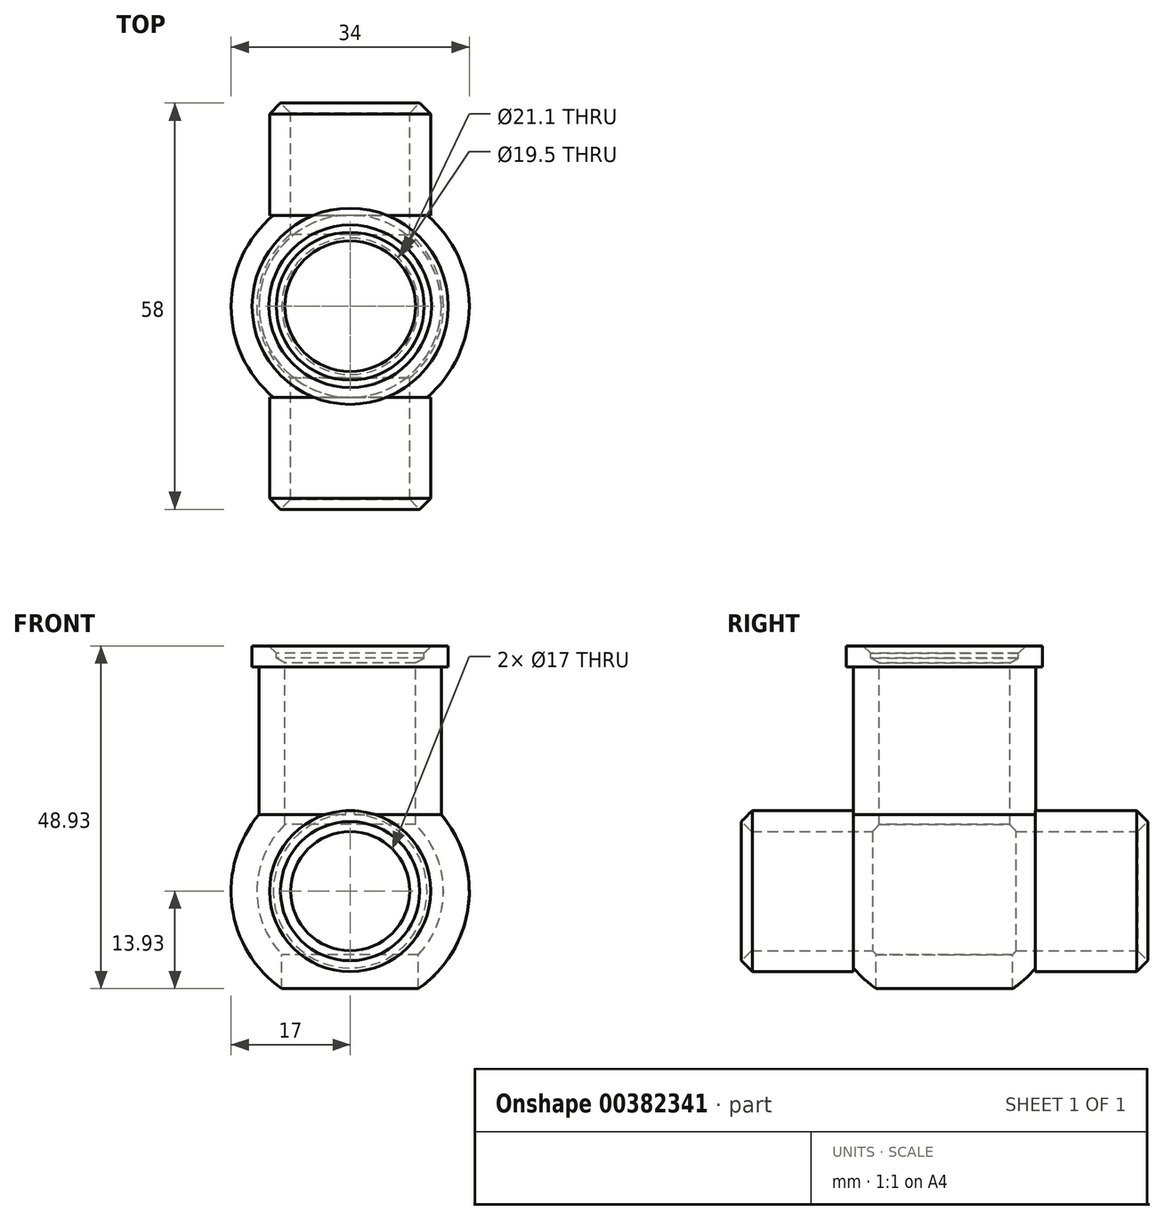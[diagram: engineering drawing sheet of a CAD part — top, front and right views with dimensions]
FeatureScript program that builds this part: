
annotation { "Feature Type Name" : "Feature", "Feature Type Description" : "" }
export const myFeature = defineFeature(function(context is Context, id is Id, definition is map)
    precondition{}
    {
        {
            var Q0;
            Q0=qCreatedBy(makeId("Front.planeOp"),FACE);
            var sketch = newSketch(context, id + "F0", { "sketchPlane" : qUnion([Q0])});
            skArc(sketch, "E0", {"start": v(-9.32, 14.22) * mm, "mid": v(-17, 0.26) * mm, "end": v(-9.75, -13.93) * mm});
            skLineSegment(sketch, "E1", {"start": v(0, 35) * mm, "end": v(0, -13.32) * mm, "construction": true});
            skLineSegment(sketch, "E2", {"start": v(0, 35) * mm, "end": v(-14, 35) * mm});
            skLineSegment(sketch, "E3", {"start": v(-14, 35) * mm, "end": v(-14, 32) * mm});
            skLineSegment(sketch, "E4", {"start": v(-14, 32) * mm, "end": v(-13, 32) * mm});
            skLineSegment(sketch, "E5", {"start": v(-13, 32) * mm, "end": v(-13, 10.95) * mm});
            skLineSegment(sketch, "E6", {"start": v(0, 35) * mm, "end": v(-11.6, 35) * mm});
            skLineSegment(sketch, "E7", {"start": v(-11.6, 35) * mm, "end": v(-10.55, 33.95) * mm});
            skLineSegment(sketch, "E8", {"start": v(-10.55, 33.95) * mm, "end": v(-10.55, 33.25) * mm});
            skLineSegment(sketch, "E9", {"start": v(-10.55, 33.95) * mm, "end": v(0, 33.95) * mm});
            skLineSegment(sketch, "E10", {"start": v(-10.55, 33.25) * mm, "end": v(0, 33.25) * mm});
            skLineSegment(sketch, "E11", {"start": v(0, 32.6) * mm, "end": v(-9.32, 32.6) * mm});
            skLineSegment(sketch, "E12", {"start": v(-10.55, 33.25) * mm, "end": v(-9.32, 32.6) * mm});
            skLineSegment(sketch, "E13", {"start": v(-9.32, 32.6) * mm, "end": v(-9.32, 9.52) * mm});
            skArc(sketch, "E14", {"start": v(-9.32, 9.52) * mm, "mid": v(-13.31, 0.31) * mm, "end": v(-9.75, -9.07) * mm});
            skLineSegment(sketch, "E15", {"start": v(-10.48, 33.21) * mm, "end": v(-10.48, 19.21) * mm});
            skLineSegment(sketch, "E16", {"start": v(-10.48, 19.21) * mm, "end": v(0, 19.21) * mm});
            skLineSegment(sketch, "E17", {"start": v(0, 13.32) * mm, "end": v(0, 17) * mm});
            skLineSegment(sketch, "E18", {"start": v(-9.75, -9.07) * mm, "end": v(-9.75, -13.93) * mm});
            skLineSegment(sketch, "E19.trimOffspring", {"start": v(0, -17) * mm, "end": v(0, -57.86) * mm, "construction": true});
            skSolve(sketch);
        }
        {
            var Q0;
            Q0=qCreatedBy(makeId("Right.planeOp"),FACE);
            var sketch = newSketch(context, id + "F1", { "sketchPlane" : qUnion([Q0])});
            skLineSegment(sketch, "E20", {"start": v(29, 0) * mm, "end": v(-20.36, 0) * mm, "construction": true});
            skLineSegment(sketch, "E21", {"start": v(29, 0) * mm, "end": v(29, 11.5) * mm});
            skLineSegment(sketch, "E22", {"start": v(29, 0) * mm, "end": v(29, -11.5) * mm});
            skLineSegment(sketch, "E23", {"start": v(29, -11.5) * mm, "end": v(0, -11.5) * mm});
            skLineSegment(sketch, "E24", {"start": v(29, 0) * mm, "end": v(29, 8.5) * mm});
            skLineSegment(sketch, "E25", {"start": v(29, 9.93) * mm, "end": v(27.57, 8.5) * mm});
            skLineSegment(sketch, "E26", {"start": v(29, 9.93) * mm, "end": v(27.43, 11.5) * mm});
            skLineSegment(sketch, "E27", {"start": v(27.43, 11.5) * mm, "end": v(0, 11.5) * mm});
            skLineSegment(sketch, "E28", {"start": v(27.57, 8.5) * mm, "end": v(0, 8.5) * mm});
            skLineSegment(sketch, "E29", {"start": v(12.99, 11.5) * mm, "end": v(12.99, 10.97) * mm});
            skArc(sketch, "E30", {"start": v(12.99, 10.97) * mm, "mid": v(13.9, 9.77) * mm, "end": v(14.72, 8.5) * mm});
            skPoint(sketch, "E31", {"position": v(17, 0) * mm});
            skArc(sketch, "E32.MirrorCS", {"start": v(-12.99, 10.97) * mm, "mid": v(-13.9, 9.77) * mm, "end": v(-14.72, 8.5) * mm});
            skLineSegment(sketch, "E33.MirrorCS", {"start": v(-27.43, 11.5) * mm, "end": v(0, 11.5) * mm});
            skLineSegment(sketch, "E34.MirrorCS", {"start": v(-12.99, 11.5) * mm, "end": v(-12.99, 10.97) * mm});
            skLineSegment(sketch, "E35.MirrorCS", {"start": v(-27.57, 8.5) * mm, "end": v(0, 8.5) * mm});
            skLineSegment(sketch, "E36.MirrorCS", {"start": v(-29, 9.93) * mm, "end": v(-27.57, 8.5) * mm});
            skLineSegment(sketch, "E37.MirrorCS", {"start": v(-29, 9.93) * mm, "end": v(-27.43, 11.5) * mm});
            skPoint(sketch, "E38", {"position": v(-20.36, 0) * mm});
            skSolve(sketch);
        }
        {
            var Q0;
            Q0=qSketchRegion(id+"F0",true);
            var Q1;
            Q1=sQuery(id+"F0.wireOp",EDGE,"E1");
            revolve(context, id + "F2", {"entities" : qUnion([Q0]), "axis" : qUnion([Q1]), "revolveType" : RevolveType.FULL});
        }
        {
            var Q0;
            {var subQ1=sQuery(id+"F1.wireOp",EDGE,"E25");Q0=makeQuery(id+"F1.imprint","IMPRINT",FACE,{"disambiguationData":[TD([[makeQuery(id+"F1.imprint","IMPRINT",EDGE,{"derivedFrom":subQ1}),-1.0]])]});}
            var Q1;
            Q1=sQuery(id+"F1.wireOp",EDGE,"E20");
            revolve(context, id + "F3", {"operationType" : NewBodyOperationType.ADD, "entities" : qUnion([Q0]), "axis" : qUnion([Q1]), "revolveType" : RevolveType.FULL});
        }
        {
            var Q0;
            {var subQ1=sQuery(id+"F1.wireOp",EDGE,"E32.MirrorCS");Q0=makeQuery(id+"F1.imprint","IMPRINT",FACE,{"disambiguationData":[TD([[makeQuery(id+"F1.imprint","IMPRINT",EDGE,{"derivedFrom":subQ1}),-1.0]])]});}
            var Q1;
            Q1=sQuery(id+"F1.wireOp",EDGE,"E20");
            revolve(context, id + "F4", {"operationType" : NewBodyOperationType.ADD, "entities" : qUnion([Q0]), "axis" : qUnion([Q1]), "revolveType" : RevolveType.FULL});
        }
        {
            var Q0;
            Q0=sQuery(id+"F0.wireOp",VERTEX,"E14.center");
            var Q1;
            Q1=makeQuery(id+"F2.opRevolve","SWEPT_BODY",BODY,{"disambiguationData":[OSD([sQuery(id+"F0.wireOp",EDGE,"E0"),sQuery(id+"F0.wireOp",EDGE,"E2"),sQuery(id+"F0.wireOp",EDGE,"E3"),sQuery(id+"F0.wireOp",EDGE,"E4"),sQuery(id+"F0.wireOp",EDGE,"E5"),sQuery(id+"F0.wireOp",EDGE,"E7"),sQuery(id+"F0.wireOp",EDGE,"E8"),sQuery(id+"F0.wireOp",EDGE,"E12"),sQuery(id+"F0.wireOp",EDGE,"E13"),sQuery(id+"F0.wireOp",EDGE,"E14"),sQuery(id+"F0.wireOp",EDGE,"E18")])]});
            hole(context, id + "F5", {"style" : HoleStyle.SIMPLE, "endStyle" : HoleEndStyle.BLIND, "oppositeDirection" : true, "holeDiameter" : 17 * mm, "holeDepth" : 29 * mm, "isTappedThrough" : true, "tappedDepth" : 12 * mm, "tapClearance" : 3, "startFromSketch" : true, "locations" : qUnion([Q0]), "scope" : qUnion([Q1])});
        }
        {
            var Q0;
            Q0=sQuery(id+"F0.wireOp",VERTEX,"E14.center");
            var Q1;
            Q1=makeQuery(id+"F2.opRevolve","SWEPT_BODY",BODY,{"disambiguationData":[OSD([sQuery(id+"F0.wireOp",EDGE,"E0"),sQuery(id+"F0.wireOp",EDGE,"E2"),sQuery(id+"F0.wireOp",EDGE,"E3"),sQuery(id+"F0.wireOp",EDGE,"E4"),sQuery(id+"F0.wireOp",EDGE,"E5"),sQuery(id+"F0.wireOp",EDGE,"E7"),sQuery(id+"F0.wireOp",EDGE,"E8"),sQuery(id+"F0.wireOp",EDGE,"E12"),sQuery(id+"F0.wireOp",EDGE,"E13"),sQuery(id+"F0.wireOp",EDGE,"E14"),sQuery(id+"F0.wireOp",EDGE,"E18")])]});
            hole(context, id + "F6", {"style" : HoleStyle.SIMPLE, "endStyle" : HoleEndStyle.BLIND, "holeDiameter" : 17 * mm, "holeDepth" : 29 * mm, "isTappedThrough" : true, "tappedDepth" : 12 * mm, "tapClearance" : 3, "startFromSketch" : true, "locations" : qUnion([Q0]), "scope" : qUnion([Q1])});
        }
    });
